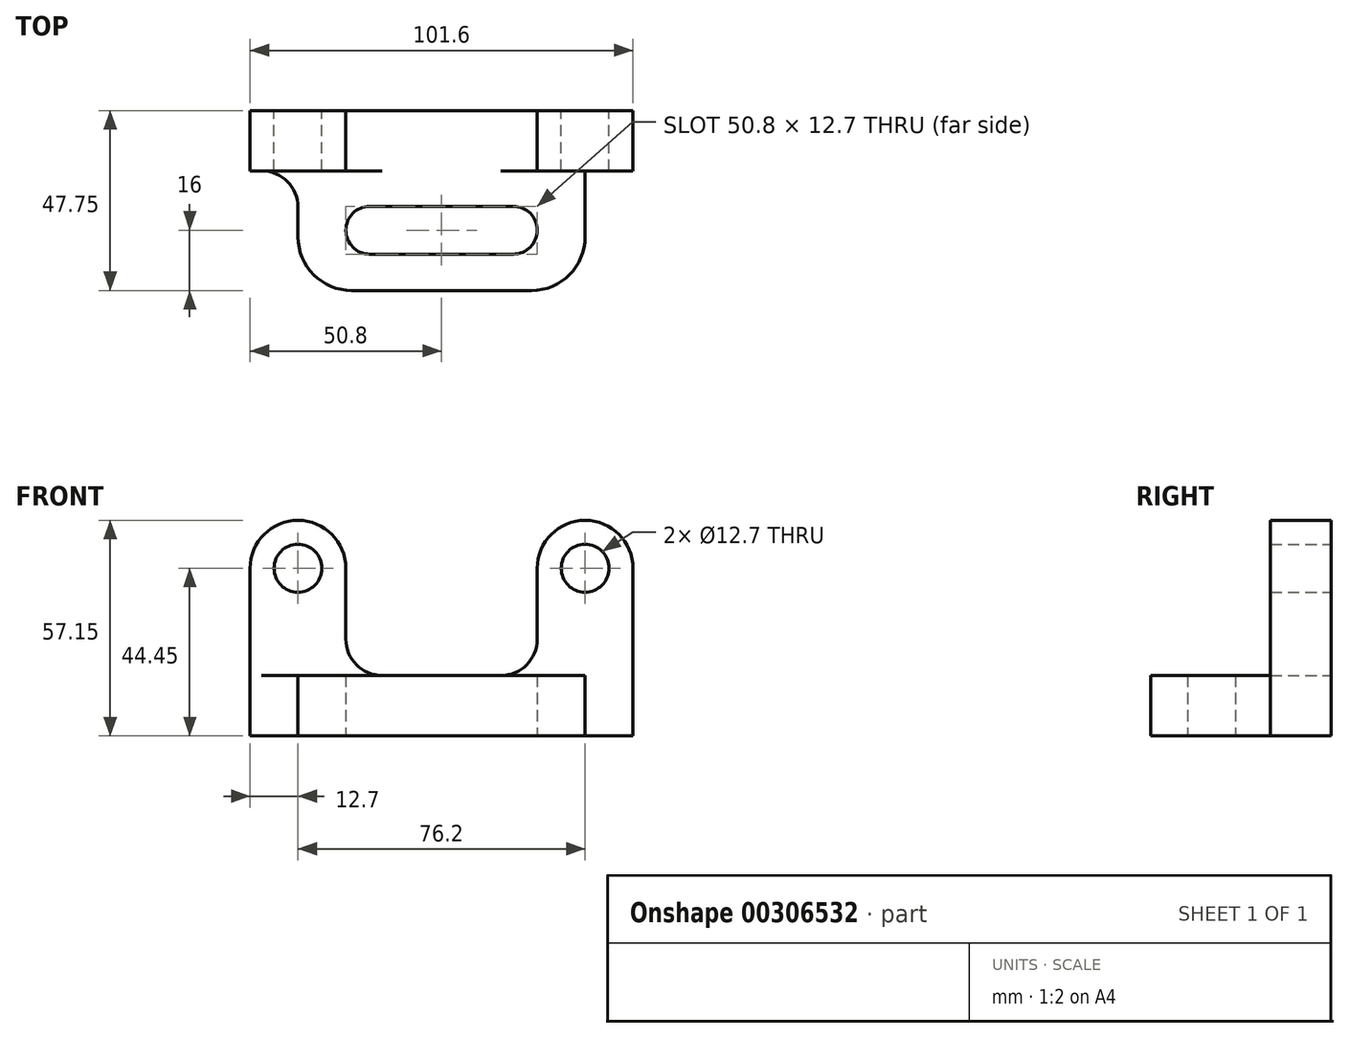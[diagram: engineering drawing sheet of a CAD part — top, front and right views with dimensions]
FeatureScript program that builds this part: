
annotation { "Feature Type Name" : "Feature", "Feature Type Description" : "" }
export const myFeature = defineFeature(function(context is Context, id is Id, definition is map)
    precondition{}
    {
        {
            var Q0;
            Q0=qCreatedBy(makeId("Front.planeOp"),FACE);
            var sketch = newSketch(context, id + "F0", { "sketchPlane" : qUnion([Q0])});
            skLineSegment(sketch, "E0", {"start": v(0, 41.44) * mm, "end": v(0, -39.27) * mm, "construction": true});
            skLineSegment(sketch, "E1", {"start": v(0, 0) * mm, "end": v(-50.8, 0) * mm});
            skCircle(sketch, "E2", {"center": v(-38.1, 44.45) * mm, "radius": 6.35 * mm});
            skLineSegment(sketch, "E3", {"start": v(-50.8, 0) * mm, "end": v(-50.8, 44.45) * mm});
            skLineSegment(sketch, "E4", {"start": v(-25.4, 44.45) * mm, "end": v(-25.4, 16) * mm});
            skArc(sketch, "E5", {"start": v(-25.4, 44.45) * mm, "mid": v(-38.1, 57.15) * mm, "end": v(-50.8, 44.45) * mm});
            skLineSegment(sketch, "E6.MirrorCS", {"start": v(25.4, 44.45) * mm, "end": v(25.4, 16) * mm});
            skLineSegment(sketch, "E7.MirrorCS", {"start": v(50.8, 0) * mm, "end": v(50.8, 44.45) * mm});
            skArc(sketch, "E8.MirrorCS", {"start": v(25.4, 44.45) * mm, "mid": v(38.1, 57.15) * mm, "end": v(50.8, 44.45) * mm});
            skCircle(sketch, "E9.MirrorC", {"center": v(38.1, 44.45) * mm, "radius": 6.35 * mm});
            skLineSegment(sketch, "E10.MirrorCS", {"start": v(0, 0) * mm, "end": v(50.8, 0) * mm});
            skLineSegment(sketch, "E11", {"start": v(-25.4, 16) * mm, "end": v(0, 16) * mm});
            skLineSegment(sketch, "E12.MirrorCS", {"start": v(25.4, 16) * mm, "end": v(0, 16) * mm});
            skSolve(sketch);
        }
        {
            var Q0;
            Q0 = qSketchRegion(id + "F0", true);
            extrude(context, id + "F1", {"entities" : qUnion([Q0]), "depth" : 16 * mm});
        }
        {
            var Q0;
            Q0=makeQuery(id+"F1.opExtrude","SWEPT_EDGE",EDGE,{"disambiguationData":[OSD([sQuery(id+"F0.wireOp",EDGE,"E4"),sQuery(id+"F0.wireOp",EDGE,"E11")])]});
            var Q1;
            Q1=makeQuery(id+"F1.opExtrude","SWEPT_EDGE",EDGE,{"disambiguationData":[OSD([sQuery(id+"F0.wireOp",EDGE,"E6.MirrorCS"),sQuery(id+"F0.wireOp",EDGE,"E12.MirrorCS")])]});
            fillet(context, id + "F2", {"entities" : qUnion([Q0, Q1]), "radius" : 9.65 * mm, "tangentPropagation" : true, "allowEdgeOverflow" : false});
        }
        {
            var Q0;
            Q0=qCreatedBy(makeId("Top.planeOp"),FACE);
            var sketch = newSketch(context, id + "F3", { "sketchPlane" : qUnion([Q0])});
            skLineSegment(sketch, "E13", {"start": v(0, 0) * mm, "end": v(0, -99.33) * mm, "construction": true});
            skLineSegment(sketch, "E14", {"start": v(0, -16) * mm, "end": v(-38.1, -16) * mm});
            skLineSegment(sketch, "E15", {"start": v(-38.1, -16) * mm, "end": v(-38.1, -33.53) * mm});
            skArc(sketch, "E16", {"start": v(-38.1, -33.53) * mm, "mid": v(-33.93, -43.59) * mm, "end": v(-23.88, -47.75) * mm});
            skLineSegment(sketch, "E17", {"start": v(-23.88, -47.75) * mm, "end": v(0, -47.75) * mm});
            skArc(sketch, "E18.MirrorCS", {"start": v(38.1, -33.53) * mm, "mid": v(33.93, -43.59) * mm, "end": v(23.88, -47.75) * mm});
            skLineSegment(sketch, "E19.MirrorCS", {"start": v(38.1, -16) * mm, "end": v(38.1, -33.53) * mm});
            skLineSegment(sketch, "E20.MirrorCS", {"start": v(23.88, -47.75) * mm, "end": v(0, -47.75) * mm});
            skLineSegment(sketch, "E21.MirrorCS", {"start": v(0, -16) * mm, "end": v(38.1, -16) * mm});
            skSolve(sketch);
        }
        {
            var Q0;
            Q0=qCreatedBy(makeId("Top.planeOp"),FACE);
            var sketch = newSketch(context, id + "F4", { "sketchPlane" : qUnion([Q0])});
            skLineSegment(sketch, "E22", {"start": v(0, -25.4) * mm, "end": v(-19.05, -25.4) * mm});
            skLineSegment(sketch, "E23", {"start": v(-19.05, -38.1) * mm, "end": v(0, -38.1) * mm});
            skArc(sketch, "E24", {"start": v(-19.05, -25.4) * mm, "mid": v(-25.4, -31.75) * mm, "end": v(-19.05, -38.1) * mm});
            skLineSegment(sketch, "E25", {"start": v(-25.4, -31.75) * mm, "end": v(30.83, -31.75) * mm, "construction": true});
            skPoint(sketch, "E25.endSnap0", {"position": v(-25.4, -31.75) * mm});
            skLineSegment(sketch, "E26.MirrorCS", {"start": v(19.05, -38.1) * mm, "end": v(0, -38.1) * mm});
            skLineSegment(sketch, "E27.MirrorCS", {"start": v(0, -25.4) * mm, "end": v(19.05, -25.4) * mm});
            skArc(sketch, "E28.MirrorCS", {"start": v(19.05, -25.4) * mm, "mid": v(25.4, -31.75) * mm, "end": v(19.05, -38.1) * mm});
            skSolve(sketch);
        }
        {
            var Q0;
            Q0 = qSketchRegion(id + "F3", true);
            extrude(context, id + "F5", {"entities" : qUnion([Q0]), "operationType" : NewBodyOperationType.ADD, "depth" : 16 * mm});
        }
        {
            var Q0;
            Q0=makeQuery(id+"F5.opExtrude","SWEPT_EDGE",EDGE,{"disambiguationData":[OSD([sQuery(id+"F3.wireOp",EDGE,"E14"),sQuery(id+"F3.wireOp",EDGE,"E15")])]});
            var Q1;
            Q1=makeQuery(id+"F5.opExtrude","SWEPT_EDGE",EDGE,{"disambiguationData":[OSD([sQuery(id+"F3.wireOp",EDGE,"E19.MirrorCS"),sQuery(id+"F3.wireOp",EDGE,"E21.MirrorCS")])]});
            fillet(context, id + "F6", {"entities" : qUnion([Q0, Q1]), "radius" : 9.65 * mm, "tangentPropagation" : true, "allowEdgeOverflow" : false});
        }
        {
            var Q0;
            Q0 = qSketchRegion(id + "F4", true);
            extrude(context, id + "F7", {"entities" : qUnion([Q0]), "operationType" : NewBodyOperationType.REMOVE, "endBound" : BoundingType.THROUGH_ALL, "depth" : 25.4 * mm});
        }
    });
